# Revit family: Sanitary_Bath-Spas_DURAVIT-AG_DuraSquare-Bathtub-White-Matt-1600x750-mm-700460_NEW
name_source: partatom
category: Plumbing Fixtures
units: mm (PartAtom-declared; Revit-internal decimal feet)

## family parameters
Cut with Voids When Loaded = Yes
Host = Face
Maintain Annotation Orientation = No
OmniClass Number = 23.31.15.00
OmniClass Title = Bathtubs
Part Type = Normal
Room Calculation Point = No
Round Connector Dimension = Use Diameter
Shared = No

## types (1)
- DuraSquare Bathtub White Matt 1600x750 mm - 700460
    Article Number = 700460000000000
    Default Elevation = 0 mm  [stored 0 ft]
    Depth = 750 mm  [stored 2.46063 ft]
    Description = Duravit DuraSquare Bathtub Rectangular Type of installation: Freestanding Seamless panel White Matt Material: Polymer cast DuroCast Plus Number of backrests: 2 Incl. support frame Incl. waste and overflow Overflow: Yes Waste outlet position: Middle Overflow position: Middle Capacity: 160 l Internal depth: 460 mm - 700460000000000
    Diameter = 52 mm
    Height = 485 mm  [stored 1.59121 ft]
    Installation instructions = https://duravit-public-assets.s3.eu-central-1.amazonaws.com
    Manufacturer = Duravit
    Material 1 = Duravit - Polymer - 00 - White Alpin
    Material 2 = Duravit - Metal - 10 - Chrome
    Model = DuraSquare Bathtub 1600x750 mm - 700460
    Product Documentation Link = https://pro.duravit.com
    Product Page URL = https://pro.duravit.com
    Product data url = https://bimobject.com
    URL = https://www.duravit.com
    Version = 1
    Weight = 109.00 kg
    Width = 1600 mm  [stored 5.24934 ft]

note: [stored X ft] marks values corroborated as IEEE doubles in the binary element streams (Revit-internal decimal feet)

## geometry (parser evidence)
native form markers: Sweep x1
no freeform markers — native parametric forms only
